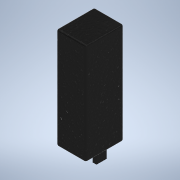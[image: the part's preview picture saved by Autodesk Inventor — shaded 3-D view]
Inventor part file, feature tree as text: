
AUTODESK INVENTOR PART (.ipt)
format: ipt  version: 2020 (Build 240168000, 168)  size: 131,584 bytes
history: native  units: mm
features: extrude x2, sketch x2, fillet x1
ambient origin geometry x8: Origin, YZ Plane, XZ Plane, XY Plane, X Axis, Y Axis, Z Axis, Center Point
bodies: Solid1 (feature_tree)
feature tree (5):
  extrude  "Extrusion1"  Depth=33.5mm
  fillet  "Fillet1"  Radius=43.0mm
  extrude  "Extrusion2"  Depth=10.0mm TaperAngle=0.0deg
  sketch  "Sketch1"  dims[d0=115.0mm d1=33.5mm d2=43.0mm d3=0.0mm]
  sketch  "Sketch2"  dims[d4=2.0mm d5=10.0mm d6=0.0mm]
